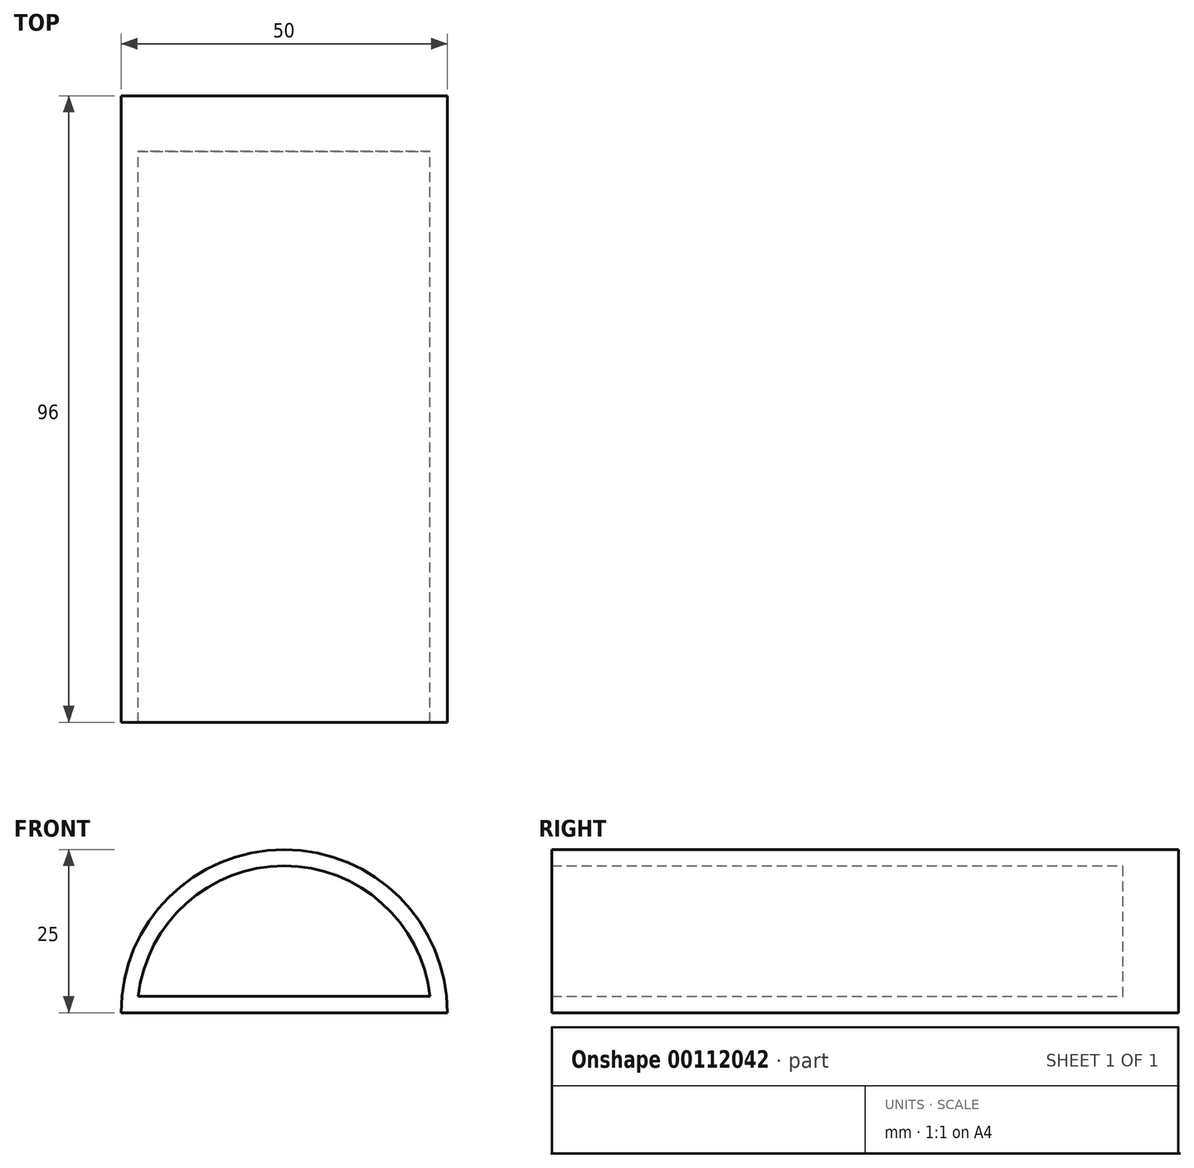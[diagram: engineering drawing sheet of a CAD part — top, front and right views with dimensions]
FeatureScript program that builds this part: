
annotation { "Feature Type Name" : "Feature", "Feature Type Description" : "" }
export const myFeature = defineFeature(function(context is Context, id is Id, definition is map)
    precondition{}
    {
        {
            var Q0;
            Q0=qCreatedBy(makeId("Front.planeOp"),FACE);
            var sketch = newSketch(context, id + "F0", { "sketchPlane" : qUnion([Q0])});
            skArc(sketch, "E0", {"start": v(25, 0) * mm, "mid": v(0, 25) * mm, "end": v(-25, 0) * mm});
            skLineSegment(sketch, "E1", {"start": v(-25, 0) * mm, "end": v(25, 0) * mm});
            skSolve(sketch);
        }
        {
            var Q0;
            Q0=makeQuery(id+"F0.imprint","IMPRINT",FACE,{"disambiguationData":[TD([[makeQuery(id+"F0.imprint","IMPRINT",EDGE,{"derivedFrom":sQuery(id+"F0.wireOp",EDGE,"E0")}),1.0]])]});
            extrude(context, id + "F1", {"entities" : qUnion([Q0]), "depth" : 90 * mm});
        }
        {
            var Q0;
            Q0=makeQuery(id+"F1.opExtrude","CAP_FACE",FACE,{"disambiguationData":[OSD([sQuery(id+"F0.wireOp",EDGE,"E0")])],"isStart":false});
            var Q1;
            Q1=makeQuery(id+"F1.opExtrude","SWEPT_BODY",BODY,{"disambiguationData":[OSD([sQuery(id+"F0.wireOp",EDGE,"E0")])]});
            shell(context, id + "F2", {"entities" : qUnion([Q0]), "parts" : qUnion([Q1]), "thickness" : 2.5 * mm});
        }
        {
            var Q0;
            Q0=makeQuery(id+"F1.opExtrude","CAP_FACE",FACE,{"disambiguationData":[OSD([sQuery(id+"F0.wireOp",EDGE,"E0")])],"isStart":true});
            extrude(context, id + "F3", {"entities" : qUnion([Q0]), "operationType" : NewBodyOperationType.ADD, "depth" : 6 * mm});
        }
        {
            var Q0;
            Q0=qCreatedBy(makeId("Right.planeOp"),FACE);
            var sketch = newSketch(context, id + "F4", { "sketchPlane" : qUnion([Q0])});
            skLineSegment(sketch, "E2", {"start": v(6, 9.95) * mm, "end": v(8, 11.1) * mm});
            skLineSegment(sketch, "E3", {"start": v(6, 9.95) * mm, "end": v(6, -9.95) * mm, "construction": true});
            skLineSegment(sketch, "E4", {"start": v(8, -11.1) * mm, "end": v(6, -9.95) * mm});
            skLineSegment(sketch, "E5", {"start": v(8, 11.1) * mm, "end": v(8, -11.1) * mm, "construction": true});
            skLineSegment(sketch, "E6", {"start": v(8, 0) * mm, "end": v(6, 0) * mm, "construction": true});
            skLineSegment(sketch, "E7", {"start": v(8, -25.28) * mm, "end": v(8, 11.1) * mm});
            skLineSegment(sketch, "E8", {"start": v(6, -25.28) * mm, "end": v(8, -25.28) * mm});
            skLineSegment(sketch, "E9", {"start": v(6, 9.95) * mm, "end": v(6, -25.28) * mm});
            skLineSegment(sketch, "E10", {"start": v(8, 47.77) * mm, "end": v(8, -11.1) * mm});
            skLineSegment(sketch, "E11", {"start": v(6, 47.77) * mm, "end": v(8, 47.77) * mm});
            skLineSegment(sketch, "E12", {"start": v(6, -9.95) * mm, "end": v(6, 47.77) * mm});
            skSolve(sketch);
        }
        {
            var Q0;
            Q0=makeQuery(id+"F4.imprint","IMPRINT",FACE,{"disambiguationData":[TD([[makeQuery(id+"F4.imprint","IMPRINT",EDGE,{"derivedFrom":sQuery(id+"F4.wireOp",EDGE,"E2")}),1.0]])]});
            var Q1;
            Q1=makeQuery(id+"F4.imprint","IMPRINT",FACE,{"disambiguationData":[TD([[makeQuery(id+"F4.imprint","IMPRINT",EDGE,{"derivedFrom":sQuery(id+"F4.wireOp",EDGE,"E4")}),1.0]])]});
            extrude(context, id + "F5", {"entities" : qUnion([Q0, Q1]), "operationType" : NewBodyOperationType.REMOVE, "endBound" : BoundingType.SYMMETRIC, "depth" : 100 * mm});
        }
    });
